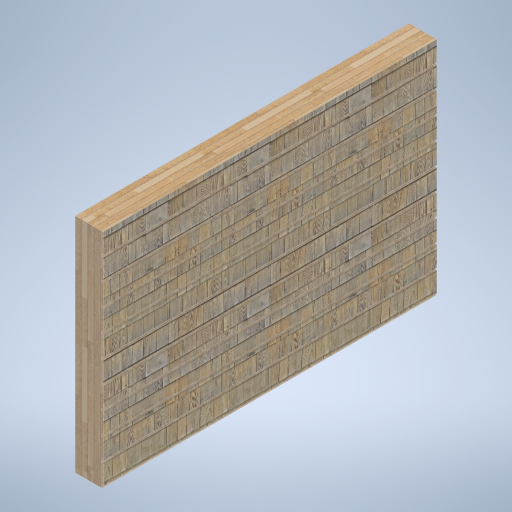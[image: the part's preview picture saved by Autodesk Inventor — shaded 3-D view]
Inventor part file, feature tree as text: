
AUTODESK INVENTOR PART (.ipt)
format: ipt  version: 2024.2 (Build 282272000, 272)  size: 544,256 bytes
history: native  units: mm
features: extrude x2, sketch x2
ambient origin geometry x8: Origin, YZ Plane, XZ Plane, XY Plane, X Axis, Y Axis, Z Axis, Center Point
bodies: Solid1 (feature_tree)
feature tree (4):
  extrude  "Extrusion1"  Depth=3000.0mm
  extrude  "Extrusion2"  Depth=250.0mm TaperAngle=0.0deg
  sketch  "Sketch1"  dims[d0=2000.0mm d1=3000.0mm]
  sketch  "Sketch3"  dims[d2=90.0deg d3=250.0mm d4=0.0mm d14=180.0mm d15=180.0mm d16=180.0mm d17=180.0mm d18=180.0mm d19=180.0mm d20=180.0mm d21=180.0mm d22=180.0mm d23=180.0mm d24=0.0mm d25=0.0mm]
